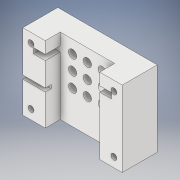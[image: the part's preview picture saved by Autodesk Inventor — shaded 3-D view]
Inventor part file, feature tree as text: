
AUTODESK INVENTOR PART (.ipt)
format: ipt  version: 2018 (Build 220112000, 112)  size: 229,376 bytes
history: native  units: in
note: dims shown in document units (in); Inventor stores cm internally (conversion verified against a paired STEP export)
features: extrude x7, sketch x7, pattern_linear x1
ambient origin geometry x8: Origin, YZ Plane, XZ Plane, XY Plane, X Axis, Y Axis, Z Axis, Center Point
bodies: Solid1 (feature_tree)
feature tree (15):
  extrude  "Cover_Body"  Depth=1.2598in
  extrude  "Servo_Opening"  Depth=0.1969in
  extrude  "Cable_Opening"  Depth=0.0906in
  extrude  "Cover_Mounting_Holes"  Depth=0.0984in TaperAngle=0.0deg
  extrude  "Slot_Mounting_ScrewsHead"  Depth=1.6535in
  extrude  "Heat_Dissipation_Hole"  Depth=0.1969in
  pattern_linear  "Pattern_Heat_Dissipation_Hole"  Spacing1=0.0984in  [1 undecoded]
  extrude  "Material reduction for PLA printing only"  Depth=0.0984in
  sketch  "Sketch2"  dims[d0=1.6535in d1=1.2598in]
  sketch  "Sketch4"  dims[d2=0.622in d3=0.0in d6=0.1969in]
  sketch  "Sketch5"  dims[d14=0.0906in d15=0.0906in]
  sketch  "Sketch6"  dims[d16=0.248in d17=0.0in d20=0.0984in d21=0.0in]
  sketch  "Sketch16"  dims[d22=1.6535in d23=0.8268in]
  sketch  "Sketch17"  dims[d24=0.9055in d28=0.1969in]
  sketch  "Sketch20"  dims[d29=0.0984in d30=0.0984in d31=0.0984in d32=0.0984in d33=1.6535in d34=0.8268in d35=1.2598in d36=0.6299in d37=1.378in d38=0.689in d39=0.9449in d40=0.4724in d41=0.0787in d42=0.0in d97=0.0591in d98=0.1772in d99=0.1772in d100=0.1772in d101=0.1772in d102=0.3543in d103=0.0in d105=0.1378in d106=0.2126in d107=0.2067in d108=0.3937in d109=0.0in d110=1.1811in d112=0.2461in d113=1.1811in d115=0.2461in d118=0.9055in d119=0.4528in d120=0.4528in d121=0.9724in d124=0.0394in d125=0.0in d131=0.5197in]
note: 1 required parameter value undecoded (feature->parameter linkage not recoverable at this tier; creation-order binding heuristic only, values carry confidence <= 0.55)
